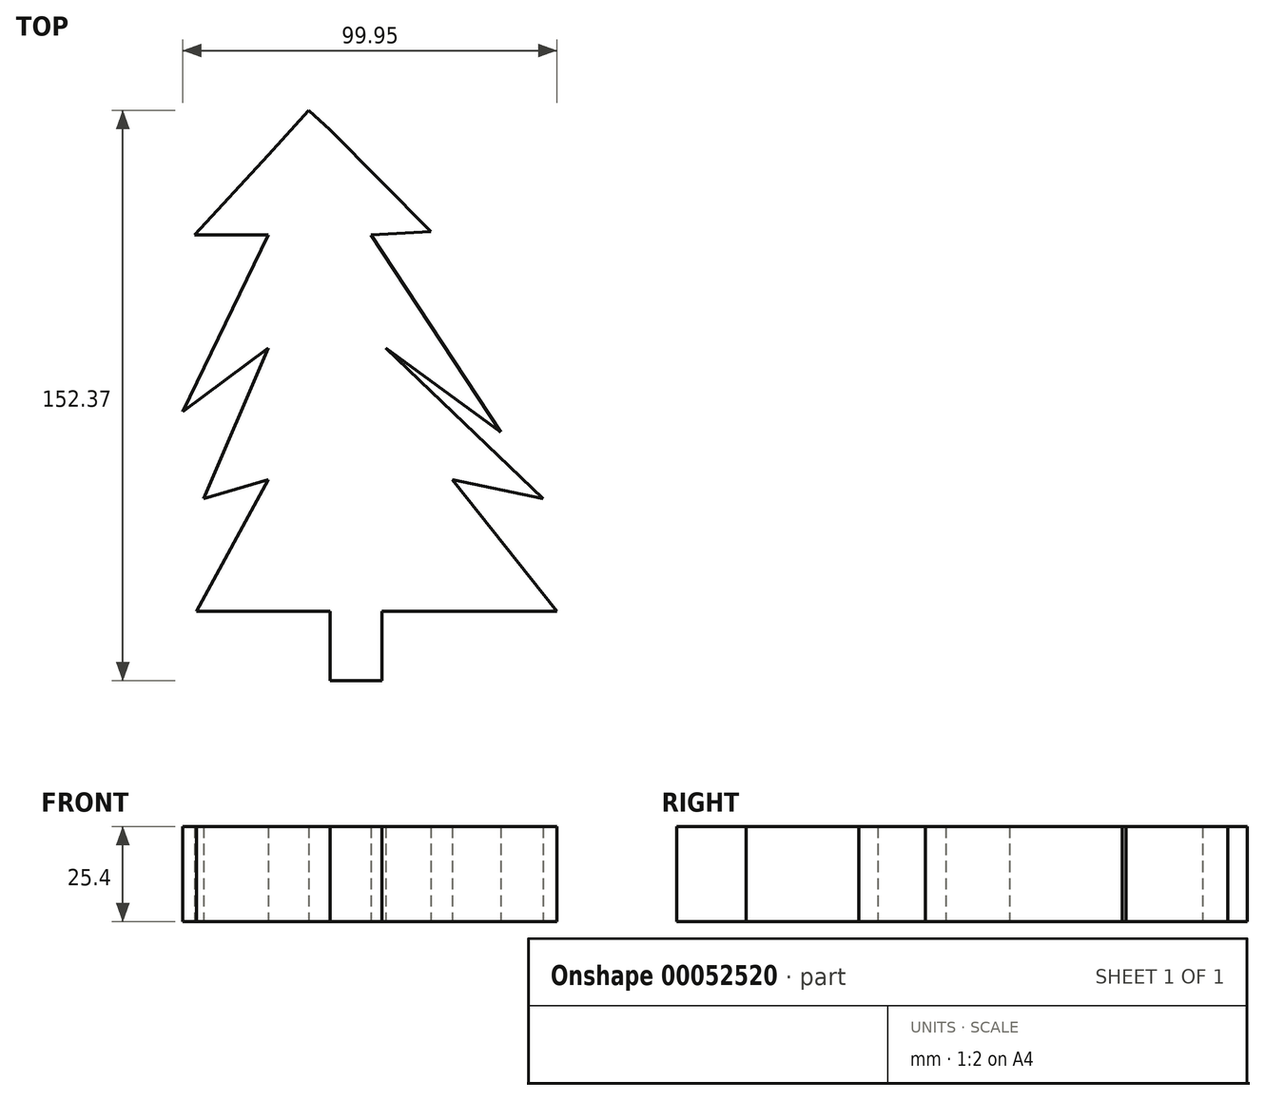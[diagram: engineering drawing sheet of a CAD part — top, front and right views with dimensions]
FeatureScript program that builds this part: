
annotation { "Feature Type Name" : "Feature", "Feature Type Description" : "" }
export const myFeature = defineFeature(function(context is Context, id is Id, definition is map)
    precondition{}
    {
        {
            var Q0;
            Q0=qCreatedBy(makeId("Top.planeOp"),FACE);
            var sketch = newSketch(context, id + "F0", { "sketchPlane" : qUnion([Q0])});
            skLineSegment(sketch, "E0", {"start": v(0, 0) * mm, "end": v(0, 18.51) * mm});
            skLineSegment(sketch, "E1", {"start": v(0, 18.51) * mm, "end": v(-35.77, 18.51) * mm});
            skLineSegment(sketch, "E2", {"start": v(-35.77, 18.51) * mm, "end": v(-16.52, 53.65) * mm});
            skLineSegment(sketch, "E3", {"start": v(-16.52, 53.65) * mm, "end": v(-33.85, 48.6) * mm});
            skLineSegment(sketch, "E4", {"start": v(-33.85, 48.6) * mm, "end": v(-16.52, 88.88) * mm});
            skLineSegment(sketch, "E5", {"start": v(-16.52, 88.88) * mm, "end": v(-39.4, 71.83) * mm});
            skLineSegment(sketch, "E6", {"start": v(-39.4, 71.83) * mm, "end": v(-16.52, 119.05) * mm});
            skLineSegment(sketch, "E7", {"start": v(-16.52, 119.05) * mm, "end": v(-36.27, 119.05) * mm});
            skLineSegment(sketch, "E8", {"start": v(-36.27, 119.05) * mm, "end": v(-16.52, 140.43) * mm});
            skLineSegment(sketch, "E9", {"start": v(0, 0) * mm, "end": v(13.73, 0) * mm});
            skLineSegment(sketch, "E10", {"start": v(-16.52, 140.43) * mm, "end": v(-5.78, 152.37) * mm});
            skLineSegment(sketch, "E11", {"start": v(-5.78, 152.37) * mm, "end": v(0, 147.17) * mm});
            skLineSegment(sketch, "E12", {"start": v(0, 147.17) * mm, "end": v(26.93, 120.04) * mm});
            skLineSegment(sketch, "E13", {"start": v(26.93, 120.04) * mm, "end": v(10.86, 119.05) * mm});
            skLineSegment(sketch, "E14", {"start": v(10.86, 119.05) * mm, "end": v(45.53, 66.35) * mm});
            skLineSegment(sketch, "E15", {"start": v(45.53, 66.35) * mm, "end": v(14.83, 88.88) * mm});
            skLineSegment(sketch, "E16", {"start": v(14.83, 88.88) * mm, "end": v(56.88, 48.6) * mm});
            skLineSegment(sketch, "E17", {"start": v(56.88, 48.6) * mm, "end": v(32.62, 53.65) * mm});
            skLineSegment(sketch, "E18", {"start": v(32.62, 53.65) * mm, "end": v(60.54, 18.51) * mm});
            skPoint(sketch, "E18.endSnap0", {"position": v(-17.88, 18.51) * mm});
            skLineSegment(sketch, "E19", {"start": v(60.54, 18.51) * mm, "end": v(13.73, 18.51) * mm});
            skLineSegment(sketch, "E20", {"start": v(13.73, 18.51) * mm, "end": v(13.73, 0) * mm});
            skSolve(sketch);
        }
        {
            var Q0;
            Q0 = qSketchRegion(id + "F0", true);
            extrude(context, id + "F1", {"entities" : qUnion([Q0]), "depth" : 25.4 * mm});
        }
    });
